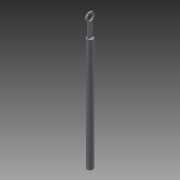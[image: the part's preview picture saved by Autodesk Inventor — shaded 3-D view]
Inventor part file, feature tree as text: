
AUTODESK INVENTOR PART (.ipt)
format: ipt  version: 2016 (Build 200138000, 138)  size: 117,248 bytes
history: native  units: in
note: dims shown in document units (in); Inventor stores cm internally (conversion verified against a paired STEP export)
features: sketch x4, extrude x3, projected_geometry x2, revolve x1
ambient origin geometry x8: Origin, YZ Plane, XZ Plane, XY Plane, X Axis, Y Axis, Z Axis, Center Point
bodies: Solid1 (feature_tree)
feature tree (10):
  revolve  "Revolution1"  Angle=90.0deg
  extrude  "Extrusion1"  Depth=3.75in
  extrude  "Extrusion2"  Depth=1.5in
  extrude  "Extrusion3"  Depth=0.25in TaperAngle=0.0deg
  sketch  "Sketch1"  dims[d0=19.0in d6=90.0deg]
  sketch  "Sketch2"  dims[d8=3.75in d9=0.0in d10=3.0in]
  sketch  "Sketch3"  dims[d11=1.0in d12=1.5in]
  projected_geometry  "Projected Loop1"
  sketch  "Sketch4"  dims[d13=0.25in d14=0.0in d15=0.25in d16=0.0in]
  projected_geometry  "Projected Loop2"
